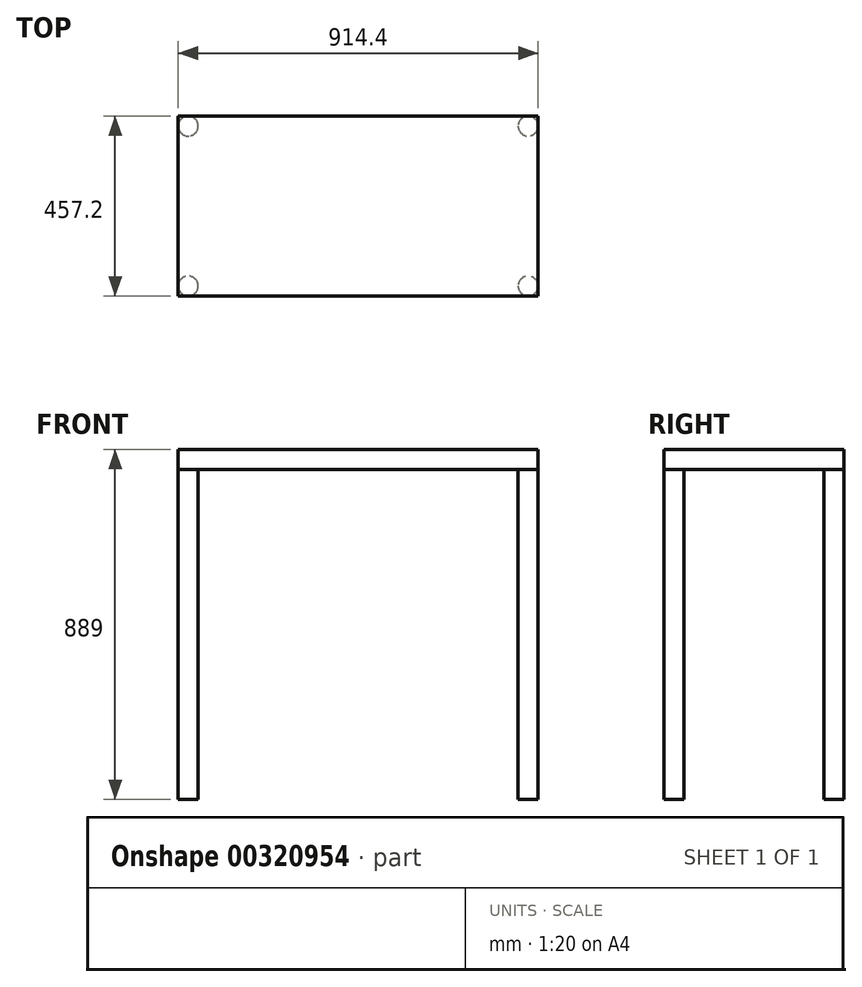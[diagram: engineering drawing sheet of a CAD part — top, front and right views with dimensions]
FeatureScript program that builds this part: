
annotation { "Feature Type Name" : "Feature", "Feature Type Description" : "" }
export const myFeature = defineFeature(function(context is Context, id is Id, definition is map)
    precondition{}
    {
        {
            var Q0;
            Q0=qCreatedBy(makeId("Top.planeOp"),FACE);
            var sketch = newSketch(context, id + "F0", { "sketchPlane" : qUnion([Q0])});
            skLineSegment(sketch, "E0.bottom", {"start": v(0, 0) * mm, "end": v(914.4, 0) * mm});
            skLineSegment(sketch, "E0.top", {"start": v(0, -457.2) * mm, "end": v(914.4, -457.2) * mm});
            skLineSegment(sketch, "E0.left", {"start": v(0, 0) * mm, "end": v(0, -457.2) * mm});
            skLineSegment(sketch, "E0.right", {"start": v(914.4, 0) * mm, "end": v(914.4, -457.2) * mm});
            skSolve(sketch);
        }
        {
            var Q0;
            Q0 = qSketchRegion(id + "F0", true);
            extrude(context, id + "F1", {"entities" : qUnion([Q0]), "depth" : 50.8 * mm});
        }
        {
            var Q0;
            Q0=makeQuery(id+"F1.opExtrude","CAP_FACE",FACE,{"disambiguationData":[OSD([sQuery(id+"F0.wireOp",EDGE,"E0.bottom"),sQuery(id+"F0.wireOp",EDGE,"E0.top"),sQuery(id+"F0.wireOp",EDGE,"E0.left"),sQuery(id+"F0.wireOp",EDGE,"E0.right")])],"isStart":true});
            var sketch = newSketch(context, id + "F2", { "sketchPlane" : qUnion([Q0])});
            skLineSegment(sketch, "E1.bottom", {"start": v(0, 457.2) * mm, "end": v(50.8, 457.2) * mm});
            skLineSegment(sketch, "E1.top", {"start": v(0, 406.4) * mm, "end": v(50.8, 406.4) * mm});
            skLineSegment(sketch, "E1.left", {"start": v(0, 457.2) * mm, "end": v(0, 406.4) * mm});
            skLineSegment(sketch, "E1.right", {"start": v(50.8, 457.2) * mm, "end": v(50.8, 406.4) * mm});
            skLineSegment(sketch, "E2.bottom", {"start": v(0, 0) * mm, "end": v(50.8, 0) * mm});
            skLineSegment(sketch, "E2.top", {"start": v(0, 50.8) * mm, "end": v(50.8, 50.8) * mm});
            skLineSegment(sketch, "E2.left", {"start": v(0, 0) * mm, "end": v(0, 50.8) * mm});
            skLineSegment(sketch, "E2.right", {"start": v(50.8, 0) * mm, "end": v(50.8, 50.8) * mm});
            skLineSegment(sketch, "E3.bottom", {"start": v(914.4, 0) * mm, "end": v(863.6, 0) * mm});
            skLineSegment(sketch, "E3.top", {"start": v(914.4, 50.8) * mm, "end": v(863.6, 50.8) * mm});
            skLineSegment(sketch, "E3.left", {"start": v(914.4, 0) * mm, "end": v(914.4, 50.8) * mm});
            skLineSegment(sketch, "E3.right", {"start": v(863.6, 0) * mm, "end": v(863.6, 50.8) * mm});
            skLineSegment(sketch, "E4.bottom", {"start": v(914.4, 457.2) * mm, "end": v(863.6, 457.2) * mm});
            skLineSegment(sketch, "E4.top", {"start": v(914.4, 406.4) * mm, "end": v(863.6, 406.4) * mm});
            skLineSegment(sketch, "E4.left", {"start": v(914.4, 457.2) * mm, "end": v(914.4, 406.4) * mm});
            skLineSegment(sketch, "E4.right", {"start": v(863.6, 457.2) * mm, "end": v(863.6, 406.4) * mm});
            skCircle(sketch, "E5", {"center": v(25.4, 431.8) * mm, "radius": 25.4 * mm});
            skPoint(sketch, "E5.centerSnap0", {"position": v(25.4, 457.2) * mm});
            skPoint(sketch, "E5.centerSnap1", {"position": v(0, 431.8) * mm});
            skCircle(sketch, "E6", {"center": v(25.4, 25.4) * mm, "radius": 25.4 * mm});
            skPoint(sketch, "E6.centerSnap0", {"position": v(0, 25.4) * mm});
            skPoint(sketch, "E6.centerSnap1", {"position": v(25.4, 50.8) * mm});
            skCircle(sketch, "E7", {"center": v(889, 25.4) * mm, "radius": 25.4 * mm});
            skPoint(sketch, "E7.centerSnap0", {"position": v(863.6, 25.4) * mm});
            skPoint(sketch, "E7.centerSnap1", {"position": v(889, 50.8) * mm});
            skCircle(sketch, "E8", {"center": v(889, 431.8) * mm, "radius": 25.4 * mm});
            skPoint(sketch, "E8.centerSnap0", {"position": v(914.4, 431.8) * mm});
            skPoint(sketch, "E8.centerSnap1", {"position": v(889, 457.2) * mm});
            skSolve(sketch);
        }
        {
            var Q0;
            {var subQ0=sQuery(id+"F2.wireOp",EDGE,"E8");var subQ1=makeQuery(id+"F2.imprint","INTERSECT",VERTEX,{"derivedFrom":[sQuery(id+"F2.wireOp",EDGE,"E4.bottom"),subQ0]});Q0=makeQuery(id+"F2.imprint","IMPRINT",FACE,{"disambiguationData":[TD([[makeQuery(id+"F2.imprint","IMPRINT",EDGE,{"disambiguationData":[TD([[subQ1,1.0]])],"derivedFrom":subQ0}),1.0]])]});}
            var Q1;
            {var subQ0=sQuery(id+"F2.wireOp",EDGE,"E7");var subQ1=makeQuery(id+"F2.imprint","INTERSECT",VERTEX,{"derivedFrom":[sQuery(id+"F2.wireOp",EDGE,"E3.left"),subQ0]});Q1=makeQuery(id+"F2.imprint","IMPRINT",FACE,{"disambiguationData":[TD([[makeQuery(id+"F2.imprint","IMPRINT",EDGE,{"disambiguationData":[TD([[subQ1,-1.0]])],"derivedFrom":subQ0}),1.0]])]});}
            var Q2;
            {var subQ0=sQuery(id+"F2.wireOp",EDGE,"E6");var subQ1=makeQuery(id+"F2.imprint","INTERSECT",VERTEX,{"derivedFrom":[sQuery(id+"F2.wireOp",EDGE,"E2.top"),subQ0]});Q2=makeQuery(id+"F2.imprint","IMPRINT",FACE,{"disambiguationData":[TD([[makeQuery(id+"F2.imprint","IMPRINT",EDGE,{"disambiguationData":[TD([[subQ1,1.0]])],"derivedFrom":subQ0}),1.0]])]});}
            var Q3;
            {var subQ0=sQuery(id+"F2.wireOp",EDGE,"E5");var subQ1=makeQuery(id+"F2.imprint","INTERSECT",VERTEX,{"derivedFrom":[sQuery(id+"F2.wireOp",EDGE,"E1.bottom"),subQ0]});Q3=makeQuery(id+"F2.imprint","IMPRINT",FACE,{"disambiguationData":[TD([[makeQuery(id+"F2.imprint","IMPRINT",EDGE,{"disambiguationData":[TD([[subQ1,1.0]])],"derivedFrom":subQ0}),1.0]])]});}
            extrude(context, id + "F3", {"entities" : qUnion([Q0, Q1, Q2, Q3]), "operationType" : NewBodyOperationType.ADD, "depth" : 838.2 * mm});
        }
    });
